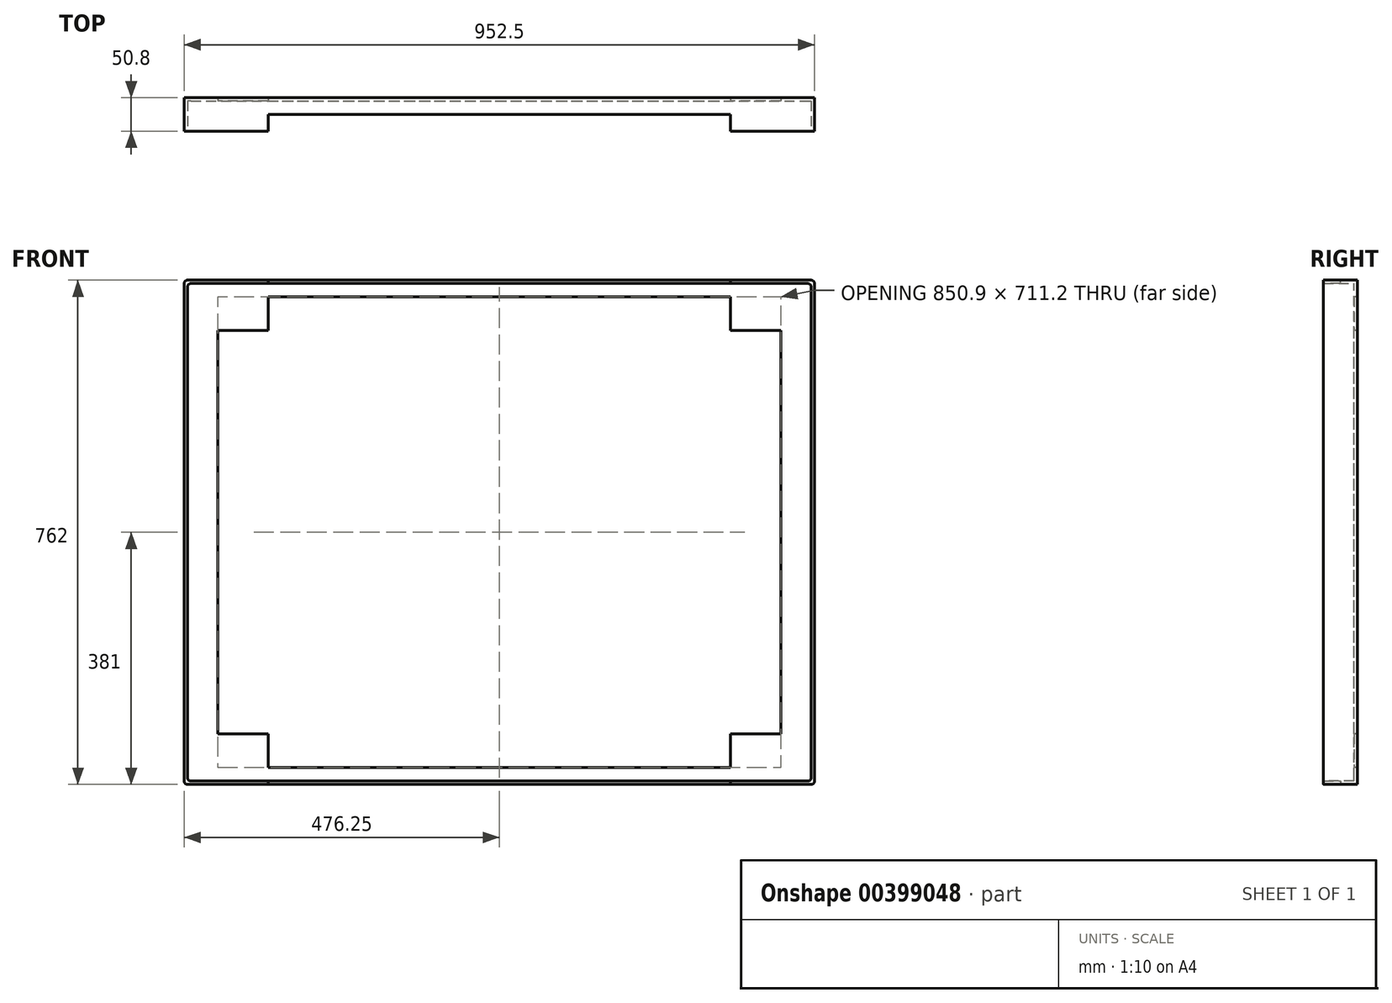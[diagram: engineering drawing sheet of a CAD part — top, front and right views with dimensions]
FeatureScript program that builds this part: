
annotation { "Feature Type Name" : "Feature", "Feature Type Description" : "" }
export const myFeature = defineFeature(function(context is Context, id is Id, definition is map)
    precondition{}
    {
        {
            var Q0;
            Q0=qCreatedBy(makeId("Front.planeOp"),FACE);
            var sketch = newSketch(context, id + "F0", { "sketchPlane" : qUnion([Q0])});
            skLineSegment(sketch, "E0", {"start": v(0, 0) * mm, "end": v(0, 762) * mm});
            skLineSegment(sketch, "E1", {"start": v(0, 762) * mm, "end": v(952.5, 762) * mm});
            skLineSegment(sketch, "E2", {"start": v(952.5, 762) * mm, "end": v(952.5, 0) * mm});
            skLineSegment(sketch, "E3", {"start": v(952.5, 0) * mm, "end": v(0, 0) * mm});
            skLineSegment(sketch, "E4.0", {"start": v(50.8, 25.4) * mm, "end": v(50.8, 736.6) * mm});
            skLineSegment(sketch, "E5.0", {"start": v(901.7, 736.6) * mm, "end": v(901.7, 25.4) * mm});
            skLineSegment(sketch, "E6.0", {"start": v(50.8, 736.6) * mm, "end": v(901.7, 736.6) * mm});
            skLineSegment(sketch, "E7.0", {"start": v(901.7, 25.4) * mm, "end": v(50.8, 25.4) * mm});
            skLineSegment(sketch, "E8", {"start": v(952.5, 762) * mm, "end": v(901.7, 711.2) * mm});
            skLineSegment(sketch, "E9", {"start": v(952.5, 0) * mm, "end": v(901.7, 50.8) * mm});
            skLineSegment(sketch, "E10", {"start": v(0, 0) * mm, "end": v(50.8, 50.8) * mm});
            skLineSegment(sketch, "E11", {"start": v(0, 762) * mm, "end": v(50.8, 711.2) * mm});
            skLineSegment(sketch, "E12", {"start": v(901.7, 736.6) * mm, "end": v(901.7, 762) * mm});
            skLineSegment(sketch, "E13", {"start": v(901.7, 25.4) * mm, "end": v(901.7, 0) * mm});
            skLineSegment(sketch, "E14", {"start": v(50.8, 25.4) * mm, "end": v(50.8, 0) * mm});
            skLineSegment(sketch, "E15", {"start": v(50.8, 736.6) * mm, "end": v(50.8, 762) * mm});
            skSolve(sketch);
        }
        {
            var Q0;
            Q0 = qSketchRegion(id + "F0", true);
            extrude(context, id + "F1", {"entities" : qUnion([Q0]), "depth" : 5.08 * mm});
        }
        {
            var Q0;
            Q0=makeQuery(id+"F1.opExtrude","SWEPT_FACE",FACE,{"disambiguationData":[OSD([sQuery(id+"F0.wireOp",EDGE,"E3")])]});
            var sketch = newSketch(context, id + "F2", { "sketchPlane" : qUnion([Q0])});
            skLineSegment(sketch, "E16", {"start": v(0, 0) * mm, "end": v(0, 50.8) * mm});
            skLineSegment(sketch, "E17", {"start": v(0, 50.8) * mm, "end": v(127, 50.8) * mm});
            skLineSegment(sketch, "E18", {"start": v(127, 50.8) * mm, "end": v(127, 25.4) * mm});
            skLineSegment(sketch, "E19", {"start": v(127, 25.4) * mm, "end": v(825.5, 25.4) * mm});
            skLineSegment(sketch, "E20", {"start": v(825.5, 25.4) * mm, "end": v(825.5, 50.8) * mm});
            skLineSegment(sketch, "E21", {"start": v(825.5, 50.8) * mm, "end": v(952.5, 50.8) * mm});
            skLineSegment(sketch, "E22", {"start": v(952.5, 50.8) * mm, "end": v(952.5, 0) * mm});
            skLineSegment(sketch, "E23", {"start": v(952.5, 0) * mm, "end": v(0, 0) * mm});
            skSolve(sketch);
        }
        {
            var Q0;
            Q0 = qSketchRegion(id + "F2", true);
            extrude(context, id + "F3", {"entities" : qUnion([Q0]), "operationType" : NewBodyOperationType.ADD, "oppositeDirection" : true, "depth" : 5.08 * mm});
        }
        {
            var Q0;
            Q0=makeQuery(id+"F1.opExtrude","SWEPT_FACE",FACE,{"disambiguationData":[OSD([sQuery(id+"F0.wireOp",EDGE,"E1")])]});
            var sketch = newSketch(context, id + "F4", { "sketchPlane" : qUnion([Q0])});
            skLineSegment(sketch, "E24", {"start": v(0, 0) * mm, "end": v(0, -50.8) * mm});
            skLineSegment(sketch, "E25", {"start": v(0, -50.8) * mm, "end": v(127, -50.8) * mm});
            skLineSegment(sketch, "E26", {"start": v(127, -50.8) * mm, "end": v(127, -25.4) * mm});
            skLineSegment(sketch, "E27", {"start": v(127, -25.4) * mm, "end": v(825.5, -25.4) * mm});
            skLineSegment(sketch, "E28", {"start": v(825.5, -25.4) * mm, "end": v(825.5, -50.8) * mm});
            skLineSegment(sketch, "E29", {"start": v(825.5, -50.8) * mm, "end": v(952.5, -50.8) * mm});
            skLineSegment(sketch, "E30", {"start": v(952.5, -50.8) * mm, "end": v(952.5, 0) * mm});
            skLineSegment(sketch, "E31", {"start": v(952.5, 0) * mm, "end": v(0, 0) * mm});
            skSolve(sketch);
        }
        {
            var Q0;
            Q0 = qSketchRegion(id + "F4", true);
            extrude(context, id + "F5", {"entities" : qUnion([Q0]), "operationType" : NewBodyOperationType.ADD, "oppositeDirection" : true, "depth" : 5.08 * mm});
        }
        {
            var Q0;
            Q0=makeQuery(id+"F5.boolean.opBoolean","MERGE",FACE,{"derivedFrom":[makeQuery(id+"F3.boolean.opBoolean","MERGE",FACE,{"derivedFrom":[makeQuery(id+"F1.opExtrude","SWEPT_FACE",FACE,{"disambiguationData":[OSD([sQuery(id+"F0.wireOp",EDGE,"E0")])]}),makeQuery(id+"F3.opExtrude","SWEPT_FACE",FACE,{"disambiguationData":[OSD([sQuery(id+"F2.wireOp",EDGE,"E16")])]})]}),makeQuery(id+"F5.opExtrude","SWEPT_FACE",FACE,{"disambiguationData":[OSD([sQuery(id+"F4.wireOp",EDGE,"E24")])]})]});
            var sketch = newSketch(context, id + "F6", { "sketchPlane" : qUnion([Q0])});
            skLineSegment(sketch, "E32", {"start": v(0, 0) * mm, "end": v(50.8, 0) * mm});
            skLineSegment(sketch, "E33", {"start": v(50.8, 0) * mm, "end": v(50.8, 762) * mm});
            skLineSegment(sketch, "E34", {"start": v(50.8, 762) * mm, "end": v(0.25, 756.92) * mm});
            skLineSegment(sketch, "E35", {"start": v(0.25, 756.92) * mm, "end": v(0.25, -5.08) * mm});
            skSolve(sketch);
        }
        {
            var Q0;
            Q0 = qSketchRegion(id + "F6", true);
            extrude(context, id + "F7", {"entities" : qUnion([Q0]), "operationType" : NewBodyOperationType.ADD, "oppositeDirection" : true, "depth" : 5.08 * mm});
        }
        {
            var Q0;
            Q0=makeQuery(id+"F5.boolean.opBoolean","MERGE",FACE,{"derivedFrom":[makeQuery(id+"F3.boolean.opBoolean","MERGE",FACE,{"derivedFrom":[makeQuery(id+"F1.opExtrude","SWEPT_FACE",FACE,{"disambiguationData":[OSD([sQuery(id+"F0.wireOp",EDGE,"E2")])]}),makeQuery(id+"F3.opExtrude","SWEPT_FACE",FACE,{"disambiguationData":[OSD([sQuery(id+"F2.wireOp",EDGE,"E22")])]})]}),makeQuery(id+"F5.opExtrude","SWEPT_FACE",FACE,{"disambiguationData":[OSD([sQuery(id+"F4.wireOp",EDGE,"E30")])]})]});
            var sketch = newSketch(context, id + "F8", { "sketchPlane" : qUnion([Q0])});
            skLineSegment(sketch, "E36", {"start": v(0, 0) * mm, "end": v(-50.8, 0) * mm});
            skLineSegment(sketch, "E37", {"start": v(-50.8, 0) * mm, "end": v(-50.8, 762) * mm});
            skLineSegment(sketch, "E38", {"start": v(-50.8, 762) * mm, "end": v(0, 762) * mm});
            skLineSegment(sketch, "E39", {"start": v(0, 762) * mm, "end": v(0, 0) * mm});
            skSolve(sketch);
        }
        {
            var Q0;
            Q0 = qSketchRegion(id + "F8", true);
            extrude(context, id + "F9", {"entities" : qUnion([Q0]), "operationType" : NewBodyOperationType.ADD, "oppositeDirection" : true, "depth" : 5.08 * mm});
        }
        {
            var Q0;
            Q0=makeQuery(id+"F3.boolean.opBoolean","MERGE",EDGE,{"derivedFrom":[makeQuery(id+"F1.opExtrude","SWEPT_EDGE",EDGE,{"disambiguationData":[OSD([sQuery(id+"F0.wireOp",EDGE,"E0"),sQuery(id+"F0.wireOp",EDGE,"E3"),sQuery(id+"F0.wireOp",EDGE,"E10")])]}),makeQuery(id+"F3.opExtrude","CAP_EDGE",EDGE,{"disambiguationData":[OSD([sQuery(id+"F2.wireOp",EDGE,"E16")])],"isStart":true})]});
            var Q1;
            Q1=makeQuery(id+"F7.boolean.opBoolean","INTERSECT",EDGE,{"derivedFrom":[makeQuery(id+"F3.opExtrude","CAP_FACE",FACE,{"disambiguationData":[OSD([sQuery(id+"F2.wireOp",EDGE,"E16"),sQuery(id+"F2.wireOp",EDGE,"E17"),sQuery(id+"F2.wireOp",EDGE,"E18"),sQuery(id+"F2.wireOp",EDGE,"E19"),sQuery(id+"F2.wireOp",EDGE,"E20"),sQuery(id+"F2.wireOp",EDGE,"E21"),sQuery(id+"F2.wireOp",EDGE,"E22"),sQuery(id+"F2.wireOp",EDGE,"E23")])],"isStart":false}),makeQuery(id+"F7.opExtrude","CAP_FACE",FACE,{"disambiguationData":[OSD([sQuery(id+"F6.wireOp",EDGE,"E32"),sQuery(id+"F6.wireOp",EDGE,"E33"),sQuery(id+"F6.wireOp",EDGE,"E34"),sQuery(id+"F6.wireOp",EDGE,"E35")])],"isStart":false})]});
            var Q2;
            Q2=makeQuery(id+"F7.boolean.opBoolean","INTERSECT",EDGE,{"derivedFrom":[makeQuery(id+"F5.opExtrude","CAP_FACE",FACE,{"disambiguationData":[OSD([sQuery(id+"F4.wireOp",EDGE,"E24"),sQuery(id+"F4.wireOp",EDGE,"E25"),sQuery(id+"F4.wireOp",EDGE,"E26"),sQuery(id+"F4.wireOp",EDGE,"E27"),sQuery(id+"F4.wireOp",EDGE,"E28"),sQuery(id+"F4.wireOp",EDGE,"E29"),sQuery(id+"F4.wireOp",EDGE,"E30"),sQuery(id+"F4.wireOp",EDGE,"E31")])],"isStart":false}),makeQuery(id+"F7.opExtrude","CAP_FACE",FACE,{"disambiguationData":[OSD([sQuery(id+"F6.wireOp",EDGE,"E32"),sQuery(id+"F6.wireOp",EDGE,"E33"),sQuery(id+"F6.wireOp",EDGE,"E34"),sQuery(id+"F6.wireOp",EDGE,"E35")])],"isStart":false})]});
            var Q3;
            Q3=makeQuery(id+"F5.boolean.opBoolean","MERGE",EDGE,{"derivedFrom":[makeQuery(id+"F1.opExtrude","SWEPT_EDGE",EDGE,{"disambiguationData":[OSD([sQuery(id+"F0.wireOp",EDGE,"E0"),sQuery(id+"F0.wireOp",EDGE,"E1"),sQuery(id+"F0.wireOp",EDGE,"E11")])]}),makeQuery(id+"F5.opExtrude","CAP_EDGE",EDGE,{"disambiguationData":[OSD([sQuery(id+"F4.wireOp",EDGE,"E24")])],"isStart":true})]});
            var Q4;
            Q4=makeQuery(id+"F5.boolean.opBoolean","MERGE",EDGE,{"derivedFrom":[makeQuery(id+"F1.opExtrude","SWEPT_EDGE",EDGE,{"disambiguationData":[OSD([sQuery(id+"F0.wireOp",EDGE,"E1"),sQuery(id+"F0.wireOp",EDGE,"E2"),sQuery(id+"F0.wireOp",EDGE,"E8")])]}),makeQuery(id+"F5.opExtrude","CAP_EDGE",EDGE,{"disambiguationData":[OSD([sQuery(id+"F4.wireOp",EDGE,"E30")])],"isStart":true})]});
            var Q5;
            Q5=makeQuery(id+"F9.boolean.opBoolean","INTERSECT",EDGE,{"derivedFrom":[makeQuery(id+"F5.opExtrude","CAP_FACE",FACE,{"disambiguationData":[OSD([sQuery(id+"F4.wireOp",EDGE,"E24"),sQuery(id+"F4.wireOp",EDGE,"E25"),sQuery(id+"F4.wireOp",EDGE,"E26"),sQuery(id+"F4.wireOp",EDGE,"E27"),sQuery(id+"F4.wireOp",EDGE,"E28"),sQuery(id+"F4.wireOp",EDGE,"E29"),sQuery(id+"F4.wireOp",EDGE,"E30"),sQuery(id+"F4.wireOp",EDGE,"E31")])],"isStart":false}),makeQuery(id+"F9.opExtrude","CAP_FACE",FACE,{"disambiguationData":[OSD([sQuery(id+"F8.wireOp",EDGE,"E36"),sQuery(id+"F8.wireOp",EDGE,"E37"),sQuery(id+"F8.wireOp",EDGE,"E38"),sQuery(id+"F8.wireOp",EDGE,"E39")])],"isStart":false})]});
            var Q6;
            Q6=makeQuery(id+"F3.boolean.opBoolean","MERGE",EDGE,{"derivedFrom":[makeQuery(id+"F1.opExtrude","SWEPT_EDGE",EDGE,{"disambiguationData":[OSD([sQuery(id+"F0.wireOp",EDGE,"E2"),sQuery(id+"F0.wireOp",EDGE,"E3"),sQuery(id+"F0.wireOp",EDGE,"E9")])]}),makeQuery(id+"F3.opExtrude","CAP_EDGE",EDGE,{"disambiguationData":[OSD([sQuery(id+"F2.wireOp",EDGE,"E22")])],"isStart":true})]});
            var Q7;
            Q7=makeQuery(id+"F9.boolean.opBoolean","INTERSECT",EDGE,{"derivedFrom":[makeQuery(id+"F3.opExtrude","CAP_FACE",FACE,{"disambiguationData":[OSD([sQuery(id+"F2.wireOp",EDGE,"E16"),sQuery(id+"F2.wireOp",EDGE,"E17"),sQuery(id+"F2.wireOp",EDGE,"E18"),sQuery(id+"F2.wireOp",EDGE,"E19"),sQuery(id+"F2.wireOp",EDGE,"E20"),sQuery(id+"F2.wireOp",EDGE,"E21"),sQuery(id+"F2.wireOp",EDGE,"E22"),sQuery(id+"F2.wireOp",EDGE,"E23")])],"isStart":false}),makeQuery(id+"F9.opExtrude","CAP_FACE",FACE,{"disambiguationData":[OSD([sQuery(id+"F8.wireOp",EDGE,"E36"),sQuery(id+"F8.wireOp",EDGE,"E37"),sQuery(id+"F8.wireOp",EDGE,"E38"),sQuery(id+"F8.wireOp",EDGE,"E39")])],"isStart":false})]});
            fillet(context, id + "F10", {"entities" : qUnion([Q0, Q1, Q2, Q3, Q4, Q5, Q6, Q7]), "radius" : 5.08 * mm, "tangentPropagation" : true, "allowEdgeOverflow" : false});
        }
        {
            var Q0;
            Q0=makeQuery(id+"F1.opExtrude","CAP_FACE",FACE,{"disambiguationData":[OSD([sQuery(id+"F0.wireOp",EDGE,"E0"),sQuery(id+"F0.wireOp",EDGE,"E1"),sQuery(id+"F0.wireOp",EDGE,"E2"),sQuery(id+"F0.wireOp",EDGE,"E3"),sQuery(id+"F0.wireOp",EDGE,"E4.0"),sQuery(id+"F0.wireOp",EDGE,"E5.0"),sQuery(id+"F0.wireOp",EDGE,"E6.0"),sQuery(id+"F0.wireOp",EDGE,"E7.0")])],"isStart":false});
            var sketch = newSketch(context, id + "F11", { "sketchPlane" : qUnion([Q0])});
            skLineSegment(sketch, "E40", {"start": v(901.7, 736.6) * mm, "end": v(901.7, 685.8) * mm});
            skLineSegment(sketch, "E41", {"start": v(901.7, 685.8) * mm, "end": v(825.5, 685.8) * mm});
            skLineSegment(sketch, "E42", {"start": v(825.5, 685.8) * mm, "end": v(825.5, 736.6) * mm});
            skLineSegment(sketch, "E43", {"start": v(825.5, 736.6) * mm, "end": v(901.7, 736.6) * mm});
            skLineSegment(sketch, "E44", {"start": v(901.7, 25.4) * mm, "end": v(901.7, 76.2) * mm});
            skLineSegment(sketch, "E45", {"start": v(901.7, 76.2) * mm, "end": v(825.5, 76.2) * mm});
            skLineSegment(sketch, "E46", {"start": v(825.5, 76.2) * mm, "end": v(825.5, 25.4) * mm});
            skLineSegment(sketch, "E47", {"start": v(825.5, 25.4) * mm, "end": v(901.7, 25.4) * mm});
            skLineSegment(sketch, "E48", {"start": v(50.8, 25.4) * mm, "end": v(127, 25.4) * mm});
            skLineSegment(sketch, "E49", {"start": v(127, 25.4) * mm, "end": v(127, 76.2) * mm});
            skLineSegment(sketch, "E50", {"start": v(127, 76.2) * mm, "end": v(50.8, 76.2) * mm});
            skLineSegment(sketch, "E51", {"start": v(50.8, 76.2) * mm, "end": v(50.8, 25.4) * mm});
            skLineSegment(sketch, "E52", {"start": v(50.8, 736.6) * mm, "end": v(127, 736.6) * mm});
            skLineSegment(sketch, "E53", {"start": v(127, 736.6) * mm, "end": v(127, 685.8) * mm});
            skLineSegment(sketch, "E54", {"start": v(127, 685.8) * mm, "end": v(50.8, 685.8) * mm});
            skLineSegment(sketch, "E55", {"start": v(50.8, 685.8) * mm, "end": v(50.8, 736.6) * mm});
            skSolve(sketch);
        }
        {
            var Q0;
            Q0 = qSketchRegion(id + "F11", true);
            extrude(context, id + "F12", {"entities" : qUnion([Q0]), "operationType" : NewBodyOperationType.ADD, "oppositeDirection" : true, "depth" : 5.08 * mm});
        }
    });
